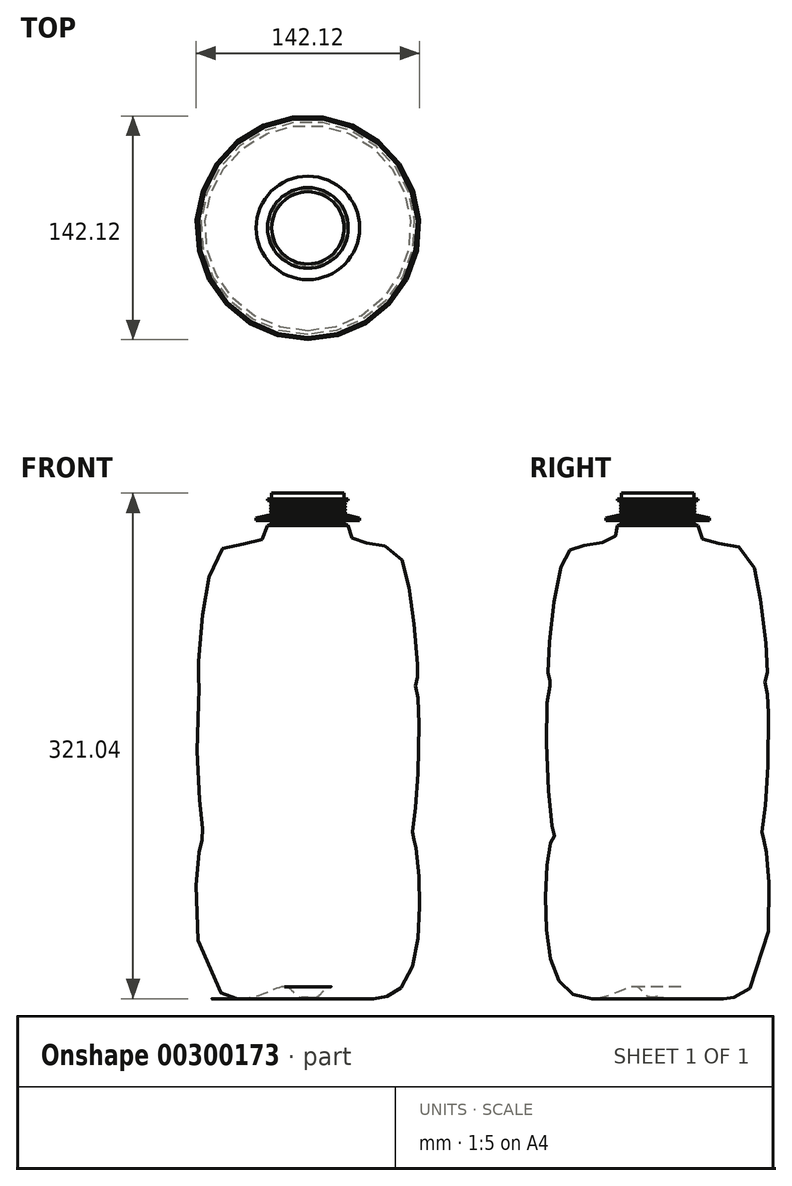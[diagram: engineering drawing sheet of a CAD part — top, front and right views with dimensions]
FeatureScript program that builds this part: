
annotation { "Feature Type Name" : "Feature", "Feature Type Description" : "" }
export const myFeature = defineFeature(function(context is Context, id is Id, definition is map)
    precondition{}
    {
        {
            var Q0;
            Q0=qCreatedBy(makeId("Right.planeOp"),FACE);
            var sketch = newSketch(context, id + "F0", { "sketchPlane" : qUnion([Q0])});
            skFitSpline(sketch, "E0", {"points": [v(0, -75.9) * mm, v(-6.51, -75.9) * mm, v(-13.29, -70.06) * mm, v(-33.85, -76.37) * mm, v(-58.39, -71.23) * mm, v(-70.77, -28) * mm, v(-67.04, 23.88) * mm, v(-65.4, 25.98) * mm, v(-66.36, 28.22) * mm, v(-69.12, 119.58) * mm, v(-67.71, 121.92) * mm, v(-68.5, 124.26) * mm, v(-69.43, 125.97) * mm, v(-60.23, 199.9) * mm, v(-48.22, 210.2) * mm, v(-27.94, 215.18) * mm, v(-25.6, 223.27) * mm], "startDerivative": vector(-181.08, -44.36) * mm, "endDerivative": vector(-2.19, 208.57) * mm});
            skLineSegment(sketch, "E1", {"start": v(0, -75.9) * mm, "end": v(0, 334.53) * mm, "construction": true});
            skLineSegment(sketch, "E2", {"start": v(-25.6, 223.27) * mm, "end": v(-22.94, 224.17) * mm});
            skLineSegment(sketch, "E3", {"start": v(-22.94, 224.17) * mm, "end": v(-22.94, 226.32) * mm});
            skLineSegment(sketch, "E4", {"start": v(-22.94, 226.32) * mm, "end": v(-32.87, 226.32) * mm});
            skLineSegment(sketch, "E5", {"start": v(-32.87, 226.32) * mm, "end": v(-32.87, 227.86) * mm});
            skLineSegment(sketch, "E6", {"start": v(-32.87, 227.86) * mm, "end": v(-22.94, 230.12) * mm});
            skLineSegment(sketch, "E7", {"start": v(-22.94, 230.12) * mm, "end": v(-23.93, 231.12) * mm});
            skLineSegment(sketch, "E8", {"start": v(-23.93, 231.12) * mm, "end": v(-22.94, 232.1) * mm});
            skLineSegment(sketch, "E9", {"start": v(-22.94, 232.1) * mm, "end": v(-23.9, 233.07) * mm});
            skLineSegment(sketch, "E10", {"start": v(-23.9, 233.07) * mm, "end": v(-22.94, 234.04) * mm});
            skLineSegment(sketch, "E11", {"start": v(-22.94, 234.04) * mm, "end": v(-23.9, 235) * mm});
            skLineSegment(sketch, "E12", {"start": v(-23.9, 235) * mm, "end": v(-22.94, 235.97) * mm});
            skLineSegment(sketch, "E13", {"start": v(-22.94, 235.97) * mm, "end": v(-23.9, 236.93) * mm});
            skLineSegment(sketch, "E14", {"start": v(-23.9, 236.93) * mm, "end": v(-22.94, 237.9) * mm});
            skLineSegment(sketch, "E15", {"start": v(-22.94, 237.9) * mm, "end": v(-22.94, 239.06) * mm});
            skLineSegment(sketch, "E16", {"start": v(-22.94, 239.06) * mm, "end": v(-25.6, 239.06) * mm});
            skLineSegment(sketch, "E17", {"start": v(-25.6, 239.06) * mm, "end": v(-25.6, 240.1) * mm});
            skLineSegment(sketch, "E18", {"start": v(-25.6, 240.1) * mm, "end": v(-22.94, 240.1) * mm});
            skLineSegment(sketch, "E19", {"start": v(-22.94, 240.1) * mm, "end": v(-22.94, 243.63) * mm});
            skLineSegment(sketch, "E20", {"start": v(-22.94, 243.63) * mm, "end": v(0, 243.63) * mm});
            skLineSegment(sketch, "E21", {"start": v(0, 243.63) * mm, "end": v(0, -75.9) * mm});
            skSolve(sketch);
        }
        {
            var Q0;
            Q0 = qSketchRegion(id + "F0", true);
            var Q1;
            Q1=sQuery(id+"F0.wireOp",EDGE,"E21");
            revolve(context, id + "F1", {"entities" : qUnion([Q0]), "axis" : qUnion([Q1]), "revolveType" : RevolveType.FULL});
        }
    });
